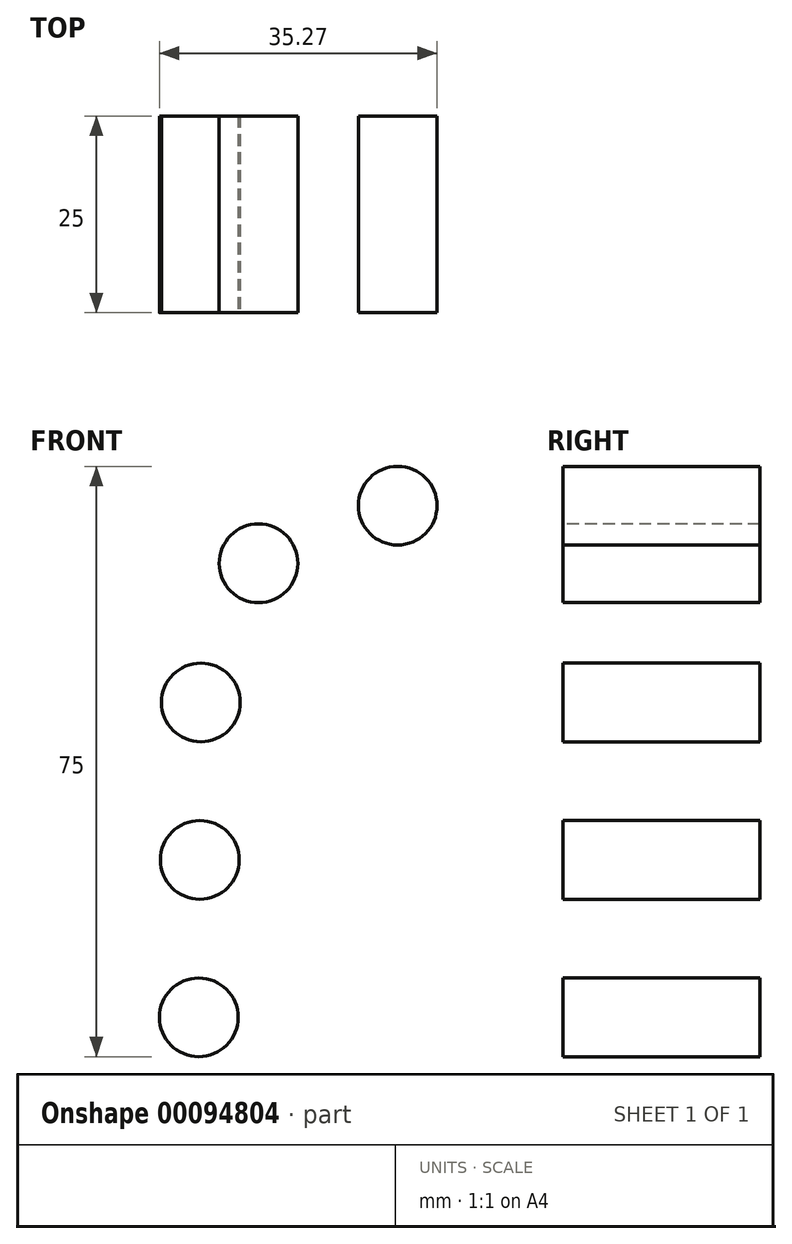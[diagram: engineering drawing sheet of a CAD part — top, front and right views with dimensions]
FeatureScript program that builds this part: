
annotation { "Feature Type Name" : "Feature", "Feature Type Description" : "" }
export const myFeature = defineFeature(function(context is Context, id is Id, definition is map)
    precondition{}
    {
        {
            var Q0;
            Q0=qCreatedBy(makeId("Front.planeOp"),FACE);
            var sketch = newSketch(context, id + "F0", { "sketchPlane" : qUnion([Q0])});
            skLineSegment(sketch, "E0", {"start": v(-25, 0) * mm, "end": v(-25, 40) * mm, "construction": true});
            skArc(sketch, "E1", {"start": v(0, 65) * mm, "mid": v(-17.68, 57.68) * mm, "end": v(-25, 40) * mm, "construction": true});
            skArc(sketch, "E2.0.endCap", {"start": v(-12.5, 40) * mm, "mid": v(-25, 27.5) * mm, "end": v(-37.5, 40) * mm, "construction": true});
            skArc(sketch, "E2.0.left", {"start": v(0, 52.5) * mm, "mid": v(-8.84, 48.84) * mm, "end": v(-12.5, 40) * mm});
            skArc(sketch, "E2.0.right", {"start": v(0, 77.5) * mm, "mid": v(-26.52, 66.52) * mm, "end": v(-37.5, 40) * mm});
            skArc(sketch, "E2.1.endCap", {"start": v(-37.5, 40) * mm, "mid": v(-25, 52.5) * mm, "end": v(-12.5, 40) * mm, "construction": true});
            skLineSegment(sketch, "E2.1.left", {"start": v(-37.5, 0) * mm, "end": v(-37.5, 40) * mm});
            skLineSegment(sketch, "E2.1.right", {"start": v(-12.5, 0) * mm, "end": v(-12.5, 40) * mm});
            skCircle(sketch, "E3", {"center": v(-25, 40) * mm, "radius": 5 * mm});
            skCircle(sketch, "E4.0.1.0", {"center": v(-25.13, 20) * mm, "radius": 5 * mm});
            skCircle(sketch, "E4.0.2.0", {"center": v(-25.27, 0) * mm, "radius": 5 * mm});
            skLineSegment(sketch, "E4.direction1", {"start": v(-25, 40) * mm, "end": v(-8.14, 40) * mm, "construction": true});
            skLineSegment(sketch, "E4.direction2", {"start": v(-25, 40) * mm, "end": v(-25.13, 20) * mm, "construction": true});
            skCircle(sketch, "E5.1.0", {"center": v(-17.68, 57.68) * mm, "radius": 5 * mm});
            skCircle(sketch, "E5.2.0", {"center": v(0, 65) * mm, "radius": 5 * mm});
            skLineSegment(sketch, "E5.anchor1", {"start": v(0, 40) * mm, "end": v(-25, 40) * mm, "construction": true});
            skLineSegment(sketch, "E5.anchor2", {"start": v(0, 40) * mm, "end": v(0, 65) * mm, "construction": true});
            skSolve(sketch);
        }
        {
            var Q0;
            Q0=sQuery(id+"F0.wireOp",EDGE,"E5.2.0");
            var Q1;
            Q1=sQuery(id+"F0.wireOp",EDGE,"E5.1.0");
            var Q2;
            Q2=sQuery(id+"F0.wireOp",EDGE,"E4.0.1.0");
            var Q3;
            Q3=sQuery(id+"F0.wireOp",EDGE,"E4.0.2.0");
            var Q4;
            Q4=sQuery(id+"F0.wireOp",EDGE,"E3");
            extrude(context, id + "F1", {"bodyType" : ToolBodyType.SURFACE, "surfaceEntities" : qUnion([Q0, Q1, Q2, Q3, Q4]), "depth" : 25 * mm});
        }
    });
